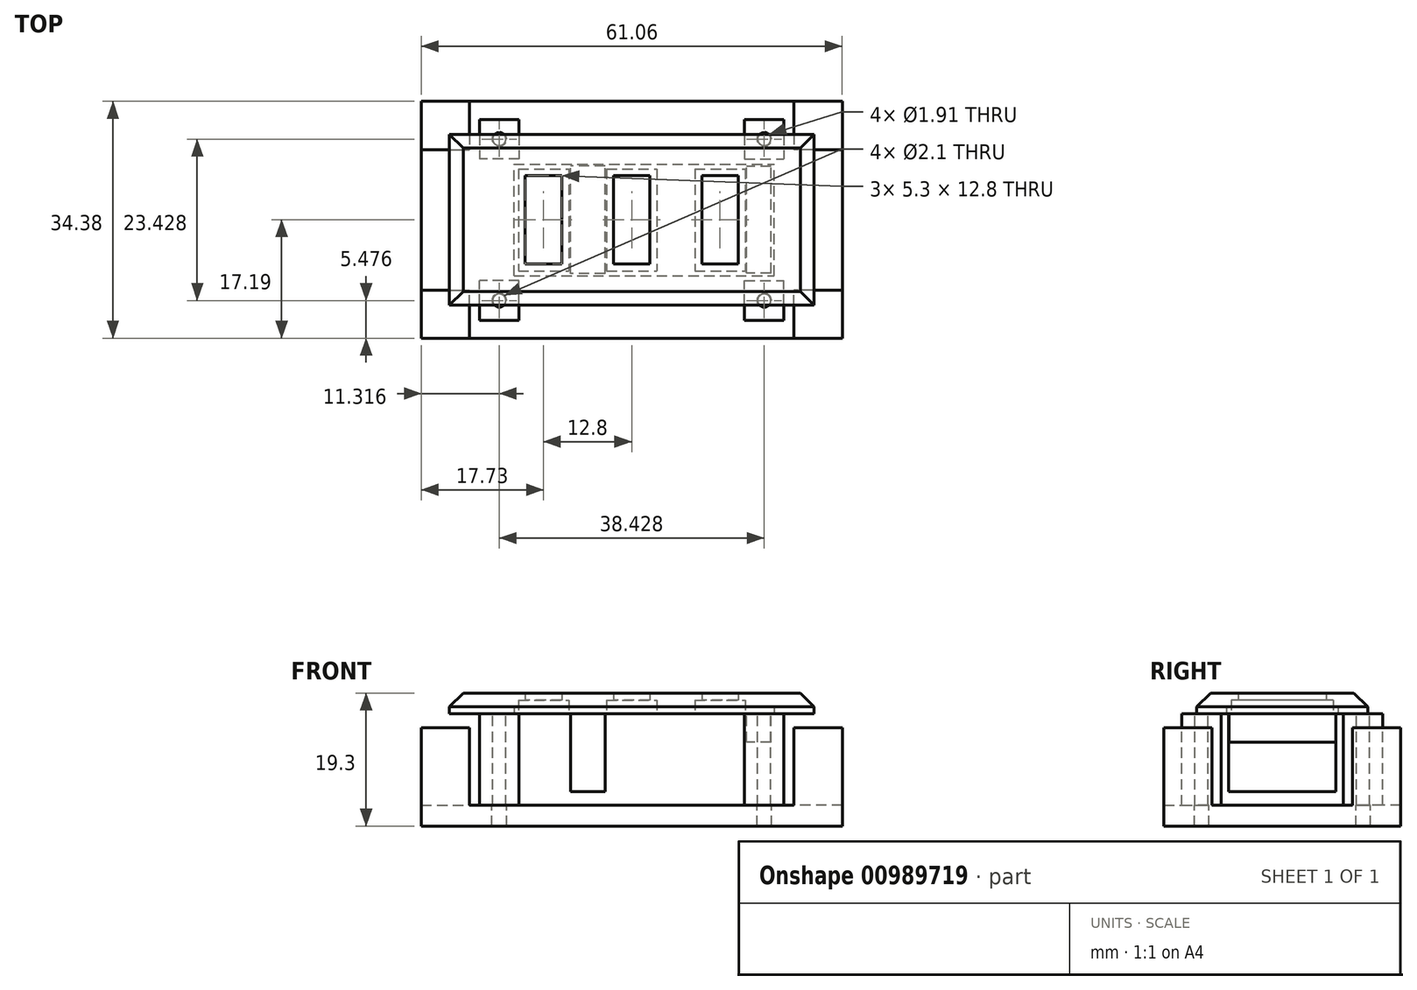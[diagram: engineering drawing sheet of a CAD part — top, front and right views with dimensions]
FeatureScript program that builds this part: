
annotation { "Feature Type Name" : "Feature", "Feature Type Description" : "" }
export const myFeature = defineFeature(function(context is Context, id is Id, definition is map)
    precondition{}
    {
        {
            assignVariable(context, id + "F0", {"name" : "usb_depth", "anyValue" : 11.1});
        }
        {
            var Q0;
            Q0=qCreatedBy(makeId("Top.planeOp"),FACE);
            var sketch = newSketch(context, id + "F1", { "sketchPlane" : qUnion([Q0])});
            skLineSegment(sketch, "E0.bottom", {"start": v(-16.45, 7.4) * mm, "end": v(-9.15, 7.4) * mm});
            skLineSegment(sketch, "E0.top", {"start": v(-16.45, -7.4) * mm, "end": v(-9.15, -7.4) * mm});
            skLineSegment(sketch, "E0.left", {"start": v(-16.45, 7.4) * mm, "end": v(-16.45, -7.4) * mm});
            skLineSegment(sketch, "E0.right", {"start": v(-9.15, 7.4) * mm, "end": v(-9.15, -7.4) * mm});
            skLineSegment(sketch, "E1.1.0.0", {"start": v(-3.65, 7.4) * mm, "end": v(-3.65, -7.4) * mm});
            skLineSegment(sketch, "E1.1.0.1", {"start": v(3.65, 7.4) * mm, "end": v(3.65, -7.4) * mm});
            skLineSegment(sketch, "E1.1.0.2", {"start": v(-3.65, 7.4) * mm, "end": v(3.65, 7.4) * mm});
            skLineSegment(sketch, "E1.1.0.3", {"start": v(-3.65, -7.4) * mm, "end": v(3.65, -7.4) * mm});
            skLineSegment(sketch, "E1.2.0.0", {"start": v(9.15, 7.4) * mm, "end": v(9.15, -7.4) * mm});
            skLineSegment(sketch, "E1.2.0.1", {"start": v(16.45, 7.4) * mm, "end": v(16.45, -7.4) * mm});
            skLineSegment(sketch, "E1.2.0.2", {"start": v(9.15, 7.4) * mm, "end": v(16.45, 7.4) * mm});
            skLineSegment(sketch, "E1.2.0.3", {"start": v(9.15, -7.4) * mm, "end": v(16.45, -7.4) * mm});
            skLineSegment(sketch, "E1.direction1", {"start": v(-16.45, -7.4) * mm, "end": v(-3.65, -7.4) * mm, "construction": true});
            skLineSegment(sketch, "E2.bottom", {"start": v(-26.45, 12.4) * mm, "end": v(26.45, 12.4) * mm});
            skLineSegment(sketch, "E2.top", {"start": v(-26.45, -12.4) * mm, "end": v(26.45, -12.4) * mm});
            skLineSegment(sketch, "E2.left", {"start": v(-26.45, 12.4) * mm, "end": v(-26.45, -12.4) * mm});
            skLineSegment(sketch, "E2.right", {"start": v(26.45, 12.4) * mm, "end": v(26.45, -12.4) * mm});
            skPoint(sketch, "E2.middle", {"position": v(0, 0) * mm});
            skSolve(sketch);
        }
        {
            var Q0;
            Q0=qCreatedBy(makeId("Top.planeOp"),FACE);
            var sketch = newSketch(context, id + "F2", { "sketchPlane" : qUnion([Q0])});
            skLineSegment(sketch, "E3.bottom", {"start": v(-28.45, 8.65) * mm, "end": v(28.45, 8.65) * mm});
            skLineSegment(sketch, "E3.top", {"start": v(-28.45, -8.65) * mm, "end": v(28.45, -8.65) * mm});
            skLineSegment(sketch, "E3.left", {"start": v(-28.45, 8.65) * mm, "end": v(-28.45, -8.65) * mm});
            skLineSegment(sketch, "E3.right", {"start": v(28.45, 8.65) * mm, "end": v(28.45, -8.65) * mm});
            skPoint(sketch, "E3.middle", {"position": v(0, 0) * mm});
            skSolve(sketch);
        }
        {
            var Q0;
            Q0 = qSketchRegion(id + "F1", true);
            var Q1;
            Q1=makeQuery(id+"F1.imprint","IMPRINT",FACE,{"disambiguationData":[TD([[makeQuery(id+"F1.imprint","IMPRINT",EDGE,{"derivedFrom":sQuery(id+"F1.wireOp",EDGE,"E0.bottom")}),-1.0]])]});
            var Q2;
            Q2=makeQuery(id+"F1.imprint","IMPRINT",FACE,{"disambiguationData":[TD([[makeQuery(id+"F1.imprint","IMPRINT",EDGE,{"derivedFrom":sQuery(id+"F1.wireOp",EDGE,"E1.1.0.0")}),1.0]])]});
            var Q3;
            Q3=makeQuery(id+"F1.imprint","IMPRINT",FACE,{"disambiguationData":[TD([[makeQuery(id+"F1.imprint","IMPRINT",EDGE,{"derivedFrom":sQuery(id+"F1.wireOp",EDGE,"E1.2.0.0")}),1.0]])]});
            extrude(context, id + "F3", {"entities" : qUnion([Q0, Q1, Q2, Q3]), "depth" : 3 * mm, "offsetDistance" : 25 * mm});
        }
        {
            var Q0;
            Q0=makeQuery(id+"F3.opExtrude","CAP_EDGE",EDGE,{"disambiguationData":[OSD([sQuery(id+"F1.wireOp",EDGE,"E2.bottom")])],"isStart":false});
            var Q1;
            Q1=makeQuery(id+"F3.opExtrude","CAP_EDGE",EDGE,{"disambiguationData":[OSD([sQuery(id+"F1.wireOp",EDGE,"E2.left")])],"isStart":false});
            var Q2;
            Q2=makeQuery(id+"F3.opExtrude","CAP_EDGE",EDGE,{"disambiguationData":[OSD([sQuery(id+"F1.wireOp",EDGE,"E2.top")])],"isStart":false});
            var Q3;
            Q3=makeQuery(id+"F3.opExtrude","CAP_EDGE",EDGE,{"disambiguationData":[OSD([sQuery(id+"F1.wireOp",EDGE,"E2.right")])],"isStart":false});
            chamfer(context, id + "F4", {"entities" : qUnion([Q0, Q1, Q2, Q3]), "width" : 2 * mm, "tangentPropagation" : true});
        }
        {
            var Q0;
            Q0=makeQuery(id+"F2.imprint","IMPRINT",FACE,{"disambiguationData":[TD([[makeQuery(id+"F2.imprint","IMPRINT",EDGE,{"derivedFrom":sQuery(id+"F2.wireOp",EDGE,"E3.bottom")}),-1.0]])]});
            var sketch = newSketch(context, id + "F5", { "sketchPlane" : qUnion([Q0])});
            skLineSegment(sketch, "E4.bottom", {"start": v(-3.88, -7.8) * mm, "end": v(-8.88, -7.8) * mm});
            skLineSegment(sketch, "E4.top", {"start": v(-3.88, 7.8) * mm, "end": v(-8.88, 7.8) * mm});
            skLineSegment(sketch, "E4.left", {"start": v(-3.88, -7.8) * mm, "end": v(-3.88, 7.8) * mm});
            skLineSegment(sketch, "E4.right", {"start": v(-8.88, -7.8) * mm, "end": v(-8.88, 7.8) * mm});
            skPoint(sketch, "E4.middle", {"position": v(-6.38, 0) * mm});
            skSolve(sketch);
        }
        {
            var Q0;
            Q0 = qSketchRegion(id + "F5", true);
            extrude(context, id + "F6", {"entities" : qUnion([Q0]), "operationType" : NewBodyOperationType.ADD, "oppositeDirection" : true, "depth" : (getVariable(context, 'usb_depth') + .2) * mm, "offsetDistance" : 25 * mm});
        }
        {
            var Q0;
            Q0=makeQuery(id+"F2.imprint","IMPRINT",FACE,{"disambiguationData":[TD([[makeQuery(id+"F2.imprint","IMPRINT",EDGE,{"derivedFrom":sQuery(id+"F2.wireOp",EDGE,"E3.bottom")}),-1.0]])]});
            var sketch = newSketch(context, id + "F7", { "sketchPlane" : qUnion([Q0])});
            skLineSegment(sketch, "E5.bottom", {"start": v(20.19, -7.74) * mm, "end": v(16.69, -7.74) * mm});
            skLineSegment(sketch, "E5.top", {"start": v(20.19, 7.74) * mm, "end": v(16.69, 7.74) * mm});
            skLineSegment(sketch, "E5.left", {"start": v(20.19, -7.74) * mm, "end": v(20.19, 7.74) * mm});
            skLineSegment(sketch, "E5.right", {"start": v(16.69, -7.74) * mm, "end": v(16.69, 7.74) * mm});
            skPoint(sketch, "E5.middle", {"position": v(18.44, 0) * mm});
            skSolve(sketch);
        }
        {
            var Q0;
            Q0 = qSketchRegion(id + "F7", true);
            extrude(context, id + "F8", {"entities" : qUnion([Q0]), "operationType" : NewBodyOperationType.ADD, "oppositeDirection" : true, "depth" : (getVariable(context, 'usb_depth') - 7) * mm, "offsetDistance" : 25 * mm});
        }
        {
            var Q0;
            Q0=makeQuery(id+"F3.opExtrude","CAP_FACE",FACE,{"disambiguationData":[OSD([sQuery(id+"F1.wireOp",EDGE,"E0.bottom"),sQuery(id+"F1.wireOp",EDGE,"E0.top"),sQuery(id+"F1.wireOp",EDGE,"E0.left"),sQuery(id+"F1.wireOp",EDGE,"E0.right"),sQuery(id+"F1.wireOp",EDGE,"E1.1.0.0"),sQuery(id+"F1.wireOp",EDGE,"E1.1.0.1"),sQuery(id+"F1.wireOp",EDGE,"E1.1.0.2"),sQuery(id+"F1.wireOp",EDGE,"E1.1.0.3"),sQuery(id+"F1.wireOp",EDGE,"E1.2.0.0"),sQuery(id+"F1.wireOp",EDGE,"E1.2.0.1"),sQuery(id+"F1.wireOp",EDGE,"E1.2.0.2"),sQuery(id+"F1.wireOp",EDGE,"E1.2.0.3"),sQuery(id+"F1.wireOp",EDGE,"E2.bottom"),sQuery(id+"F1.wireOp",EDGE,"E2.top"),sQuery(id+"F1.wireOp",EDGE,"E2.left"),sQuery(id+"F1.wireOp",EDGE,"E2.right")])],"isStart":true});
            var sketch = newSketch(context, id + "F9", { "sketchPlane" : qUnion([Q0])});
            skCircle(sketch, "E6", {"center": v(-19.21, 11.71) * mm, "radius": 0.96 * mm});
            skLineSegment(sketch, "E7.bottom", {"start": v(-16.35, 14.57) * mm, "end": v(-22.07, 14.57) * mm});
            skLineSegment(sketch, "E7.top", {"start": v(-16.35, 8.85) * mm, "end": v(-22.07, 8.85) * mm});
            skLineSegment(sketch, "E7.left", {"start": v(-16.35, 14.57) * mm, "end": v(-16.35, 8.85) * mm});
            skLineSegment(sketch, "E7.right", {"start": v(-22.07, 14.57) * mm, "end": v(-22.07, 8.85) * mm});
            skCircle(sketch, "E8.MirrorC", {"center": v(19.21, 11.71) * mm, "radius": 0.96 * mm});
            skLineSegment(sketch, "E9.MirrorCS", {"start": v(16.35, 8.85) * mm, "end": v(22.07, 8.85) * mm});
            skLineSegment(sketch, "E10.MirrorCS", {"start": v(22.07, 14.57) * mm, "end": v(22.07, 8.85) * mm});
            skLineSegment(sketch, "E11.MirrorCS", {"start": v(16.35, 14.57) * mm, "end": v(16.35, 8.85) * mm});
            skLineSegment(sketch, "E12.MirrorCS", {"start": v(16.35, 14.57) * mm, "end": v(22.07, 14.57) * mm});
            skLineSegment(sketch, "E13.MirrorCS", {"start": v(-16.35, -8.85) * mm, "end": v(-22.07, -8.85) * mm});
            skLineSegment(sketch, "E14.MirrorCS", {"start": v(16.35, -14.57) * mm, "end": v(22.07, -14.57) * mm});
            skLineSegment(sketch, "E15.MirrorCS", {"start": v(-16.35, -14.57) * mm, "end": v(-22.07, -14.57) * mm});
            skLineSegment(sketch, "E16.MirrorCS", {"start": v(16.35, -14.57) * mm, "end": v(16.35, -8.85) * mm});
            skLineSegment(sketch, "E17.MirrorCS", {"start": v(-22.07, -14.57) * mm, "end": v(-22.07, -8.85) * mm});
            skPoint(sketch, "E18.MirrorP", {"position": v(19.21, -11.71) * mm});
            skPoint(sketch, "E19.MirrorP", {"position": v(-19.21, -11.71) * mm});
            skLineSegment(sketch, "E20.MirrorCS", {"start": v(16.35, -8.85) * mm, "end": v(22.07, -8.85) * mm});
            skLineSegment(sketch, "E21.MirrorCS", {"start": v(22.07, -14.57) * mm, "end": v(22.07, -8.85) * mm});
            skCircle(sketch, "E22.MirrorC", {"center": v(-19.21, -11.71) * mm, "radius": 0.96 * mm});
            skLineSegment(sketch, "E23.MirrorCS", {"start": v(-16.35, -14.57) * mm, "end": v(-16.35, -8.85) * mm});
            skCircle(sketch, "E24.MirrorC", {"center": v(19.21, -11.71) * mm, "radius": 0.96 * mm});
            skSolve(sketch);
        }
        {
            var Q0;
            Q0 = qSketchRegion(id + "F9", true);
            extrude(context, id + "F10", {"entities" : qUnion([Q0]), "depth" : (getVariable(context, 'usb_depth') + 2.2) * mm, "offsetDistance" : 25 * mm});
        }
        {
            var Q0;
            Q0=makeQuery(id+"F10.opExtrude","CAP_FACE",FACE,{"disambiguationData":[OSD([sQuery(id+"F9.wireOp",EDGE,"E6"),sQuery(id+"F9.wireOp",EDGE,"E7.bottom"),sQuery(id+"F9.wireOp",EDGE,"E7.top"),sQuery(id+"F9.wireOp",EDGE,"E7.left"),sQuery(id+"F9.wireOp",EDGE,"E7.right")])],"isStart":false});
            var sketch = newSketch(context, id + "F11", { "sketchPlane" : qUnion([Q0])});
            skLineSegment(sketch, "E25.bottom", {"start": v(-30.53, 17.2) * mm, "end": v(30.53, 17.2) * mm});
            skLineSegment(sketch, "E25.top", {"start": v(-30.53, -17.2) * mm, "end": v(30.53, -17.2) * mm});
            skLineSegment(sketch, "E25.left", {"start": v(-30.53, 17.2) * mm, "end": v(-30.53, -17.2) * mm});
            skLineSegment(sketch, "E25.right", {"start": v(30.53, 17.2) * mm, "end": v(30.53, -17.2) * mm});
            skPoint(sketch, "E25.middle", {"position": v(0, 0) * mm});
            skCircle(sketch, "E26", {"center": v(-19.21, 11.71) * mm, "radius": 1.05 * mm});
            skCircle(sketch, "E27.MirrorC", {"center": v(19.21, 11.71) * mm, "radius": 1.05 * mm});
            skCircle(sketch, "E28.MirrorC", {"center": v(19.21, -11.71) * mm, "radius": 1.05 * mm});
            skCircle(sketch, "E29.MirrorC", {"center": v(-19.21, -11.71) * mm, "radius": 1.05 * mm});
            skSolve(sketch);
        }
        {
            var Q0;
            Q0=makeQuery(id+"F11.imprint","IMPRINT",FACE,{"disambiguationData":[TD([[makeQuery(id+"F11.imprint","IMPRINT",EDGE,{"derivedFrom":sQuery(id+"F11.wireOp",EDGE,"E25.bottom")}),-1.0]])]});
            var Q1;
            Q1=makeQuery(id+"F11.imprint","IMPRINT",FACE,{"disambiguationData":[TD([[makeQuery(id+"F11.imprint","IMPRINT",EDGE,{"derivedFrom":sQuery(id+"F11.wireOp",EDGE,"E26")}),-1.0]])]});
            extrude(context, id + "F12", {"entities" : qUnion([Q0, Q1]), "depth" : 3 * mm, "offsetDistance" : 25 * mm});
        }
        {
            var Q0;
            Q0=makeQuery(id+"F12.opExtrude","CAP_FACE",FACE,{"disambiguationData":[OSD([sQuery(id+"F11.wireOp",EDGE,"E25.bottom"),sQuery(id+"F11.wireOp",EDGE,"E25.top"),sQuery(id+"F11.wireOp",EDGE,"E25.left"),sQuery(id+"F11.wireOp",EDGE,"E25.right"),sQuery(id+"F11.wireOp",EDGE,"E26"),sQuery(id+"F11.wireOp",EDGE,"E27.MirrorC"),sQuery(id+"F11.wireOp",EDGE,"E28.MirrorC"),sQuery(id+"F11.wireOp",EDGE,"E29.MirrorC")])],"isStart":true});
            var sketch = newSketch(context, id + "F13", { "sketchPlane" : qUnion([Q0])});
            skLineSegment(sketch, "E30.bottom", {"start": v(-30.53, 17.2) * mm, "end": v(-23.53, 17.2) * mm});
            skLineSegment(sketch, "E30.top", {"start": v(-30.53, 10.2) * mm, "end": v(-23.53, 10.2) * mm});
            skLineSegment(sketch, "E30.left", {"start": v(-30.53, 17.2) * mm, "end": v(-30.53, 10.2) * mm});
            skLineSegment(sketch, "E30.right", {"start": v(-23.53, 17.2) * mm, "end": v(-23.53, 10.2) * mm});
            skLineSegment(sketch, "E31.MirrorCS", {"start": v(23.53, 17.2) * mm, "end": v(23.53, 10.2) * mm});
            skLineSegment(sketch, "E32.MirrorCS", {"start": v(30.53, 10.2) * mm, "end": v(23.53, 10.2) * mm});
            skLineSegment(sketch, "E33.MirrorCS", {"start": v(30.53, 17.2) * mm, "end": v(23.53, 17.2) * mm});
            skLineSegment(sketch, "E34.MirrorCS", {"start": v(30.53, 17.2) * mm, "end": v(30.53, 10.2) * mm});
            skLineSegment(sketch, "E35.MirrorCS", {"start": v(30.53, -17.2) * mm, "end": v(30.53, -10.2) * mm});
            skLineSegment(sketch, "E36.MirrorCS", {"start": v(-30.53, -17.2) * mm, "end": v(-23.53, -17.2) * mm});
            skLineSegment(sketch, "E37.MirrorCS", {"start": v(-23.53, -17.2) * mm, "end": v(-23.53, -10.2) * mm});
            skLineSegment(sketch, "E38.MirrorCS", {"start": v(-30.53, -10.2) * mm, "end": v(-23.53, -10.2) * mm});
            skLineSegment(sketch, "E39.MirrorCS", {"start": v(30.53, -10.2) * mm, "end": v(23.53, -10.2) * mm});
            skLineSegment(sketch, "E40.MirrorCS", {"start": v(23.53, -17.2) * mm, "end": v(23.53, -10.2) * mm});
            skLineSegment(sketch, "E41.MirrorCS", {"start": v(-30.53, -17.2) * mm, "end": v(-30.53, -10.2) * mm});
            skLineSegment(sketch, "E42.MirrorCS", {"start": v(30.53, -17.2) * mm, "end": v(23.53, -17.2) * mm});
            skSolve(sketch);
        }
        {
            assignVariable(context, id + "F14", {"name" : "panel_width", "anyValue" : 2});
        }
        {
            var Q0;
            Q0 = qSketchRegion(id + "F13", true);
            extrude(context, id + "F15", {"entities" : qUnion([Q0]), "operationType" : NewBodyOperationType.ADD, "depth" : (getVariable(context, 'usb_depth') + 2.2 - getVariable(context, 'panel_width')) * mm, "offsetDistance" : 25 * mm});
        }
        {
            var Q0;
            Q0=qCreatedBy(makeId("Top.planeOp"),FACE);
            var Q1;
            Q1=qCreatedBy(makeId("Top.planeOp"),FACE);
            var Q2;
            Q2=qCreatedBy(makeId("Top.planeOp"),FACE);
            var sketch = newSketch(context, id + "F16", { "sketchPlane" : qUnion([Q0, Q1, Q2])});
            skLineSegment(sketch, "E43.0", {"start": v(-15.45, 6.4) * mm, "end": v(-15.45, -6.4) * mm});
            skLineSegment(sketch, "E43.1", {"start": v(-10.15, 6.4) * mm, "end": v(-15.45, 6.4) * mm});
            skLineSegment(sketch, "E43.2", {"start": v(-10.15, -6.4) * mm, "end": v(-10.15, 6.4) * mm});
            skLineSegment(sketch, "E43.3", {"start": v(-15.45, -6.4) * mm, "end": v(-10.15, -6.4) * mm});
            skLineSegment(sketch, "E44.1.0.0", {"start": v(-2.65, 6.4) * mm, "end": v(-2.65, -6.4) * mm});
            skLineSegment(sketch, "E44.1.0.1", {"start": v(2.65, 6.4) * mm, "end": v(-2.65, 6.4) * mm});
            skLineSegment(sketch, "E44.1.0.2", {"start": v(2.65, -6.4) * mm, "end": v(2.65, 6.4) * mm});
            skLineSegment(sketch, "E44.1.0.3", {"start": v(-2.65, -6.4) * mm, "end": v(2.65, -6.4) * mm});
            skLineSegment(sketch, "E44.2.0.0", {"start": v(10.15, 6.4) * mm, "end": v(10.15, -6.4) * mm});
            skLineSegment(sketch, "E44.2.0.1", {"start": v(15.45, 6.4) * mm, "end": v(10.15, 6.4) * mm});
            skLineSegment(sketch, "E44.2.0.2", {"start": v(15.45, -6.4) * mm, "end": v(15.45, 6.4) * mm});
            skLineSegment(sketch, "E44.2.0.3", {"start": v(10.15, -6.4) * mm, "end": v(15.45, -6.4) * mm});
            skLineSegment(sketch, "E44.direction1", {"start": v(-15.45, -6.4) * mm, "end": v(-2.65, -6.4) * mm, "construction": true});
            skSolve(sketch);
        }
        {
            var Q0;
            Q0 = qSketchRegion(id + "F16", true);
            extrude(context, id + "F17", {"entities" : qUnion([Q0]), "operationType" : NewBodyOperationType.REMOVE, "depth" : 3 * mm, "offsetDistance" : 25 * mm});
        }
        {
            var Q0;
            Q0=makeQuery(id+"F1.imprint","IMPRINT",FACE,{"disambiguationData":[TD([[makeQuery(id+"F1.imprint","IMPRINT",EDGE,{"derivedFrom":sQuery(id+"F1.wireOp",EDGE,"E0.bottom")}),-1.0]])]});
            var Q1;
            Q1=makeQuery(id+"F1.imprint","IMPRINT",FACE,{"disambiguationData":[TD([[makeQuery(id+"F1.imprint","IMPRINT",EDGE,{"derivedFrom":sQuery(id+"F1.wireOp",EDGE,"E1.1.0.0")}),1.0]])]});
            var Q2;
            Q2=makeQuery(id+"F1.imprint","IMPRINT",FACE,{"disambiguationData":[TD([[makeQuery(id+"F1.imprint","IMPRINT",EDGE,{"derivedFrom":sQuery(id+"F1.wireOp",EDGE,"E1.2.0.0")}),1.0]])]});
            extrude(context, id + "F18", {"entities" : qUnion([Q0, Q1, Q2]), "operationType" : NewBodyOperationType.REMOVE, "depth" : 2 * mm, "offsetDistance" : 25 * mm});
        }
        {
            var Q0;
            Q0=qCreatedBy(makeId("Top.planeOp"),FACE);
            var sketch = newSketch(context, id + "F19", { "sketchPlane" : qUnion([Q0])});
            skLineSegment(sketch, "E45.bottom", {"start": v(-17.09, -8.13) * mm, "end": v(20.66, -8.13) * mm});
            skLineSegment(sketch, "E45.top", {"start": v(-17.09, 8.09) * mm, "end": v(20.66, 8.09) * mm});
            skLineSegment(sketch, "E45.left", {"start": v(-17.09, -8.13) * mm, "end": v(-17.09, 8.09) * mm});
            skLineSegment(sketch, "E45.right", {"start": v(20.66, -8.13) * mm, "end": v(20.66, 8.09) * mm});
            skSolve(sketch);
        }
        {
            var Q0;
            Q0 = qSketchRegion(id + "F19", true);
            extrude(context, id + "F20", {"entities" : qUnion([Q0]), "depth" : 1 * mm, "offsetDistance" : 25 * mm});
        }
    });
